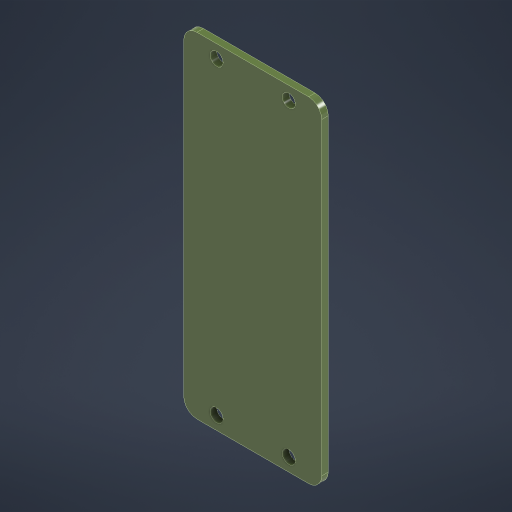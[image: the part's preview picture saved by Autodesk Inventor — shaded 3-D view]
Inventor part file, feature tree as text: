
AUTODESK INVENTOR PART (.ipt)
format: ipt  version: 2023.2 (Build 272271000, 271)  size: 221,696 bytes
history: native  units: mm
features: sketch x1
ambient origin geometry x8: Origin, YZ Plane, XZ Plane, XY Plane, X Axis, Y Axis, Z Axis, Center Point
bodies: Body1 (feature_tree)
feature tree (1):
  sketch  "Sketch1"  dims[d228=21.0mm d229=51.0mm d230=1.0mm d231=0.0mm d233=2.0mm d234=2.0mm d235=5.0mm d236=2.0mm d240=1.0mm d241=0.0mm d9=0.5mm d10=0.872665mm d11=0.5mm d12=0.872665mm d13=0.5mm d14=0.872665mm d27=0.5mm d28=0.872665mm d29=0.5mm d30=0.872665mm d88=0.5mm d89=0.872665mm d90=0.5mm d91=0.872665mm d116=0.5mm d117=0.872665mm d118=0.5mm d119=0.872665mm d154=0.5mm d155=0.872665mm d156=0.5mm d157=0.872665mm d181=0.5mm d182=0.872665mm d183=0.5mm d184=0.872665mm d221=0.5mm d222=0.872665mm d223=0.5mm d224=0.872665mm]
